# Revit family: NLRS_33_RB_DO_BILCO_dakluik_GS-50TB
name_source: partatom
category: Doors
revit_build: Autodesk Revit 2015 (Build: 20140223_1515(x64)
units: mm (PartAtom-declared; Revit-internal decimal feet)

## types (1)
- NLRS_33_RB_DO_BILCO_dakluik_GS-50TB
    Description = standaard dakluik met polycarbonaat koepel
    Height = 535 mm
    Length = 1040 mm  [stored 3.41207 ft]
    Manufacturer = Bilco
    RWA = No
    Rough Height = 0 mm  [stored 0 ft]
    Rough Width = 0 mm  [stored 0 ft]
    Thickness = 0 mm  [stored 0 ft]
    Width = 1195 mm  [stored 3.9206 ft]
    bediening = handmatig
    belasting = 195.00 kg/m²
    brandwerend 120 min = No
    brandwerend 30 min = No
    brandwerend 60 min = No
    brandwerend 90 min = No
    breedte = 1195 mm  [stored 3.9206 ft]
    breedte_koepel = 981 mm  [stored 3.2185 ft]
    breedte_paneel = 1105 mm  [stored 3.62533 ft]
    cilinderslot = No
    code productgroep = dakluiken
    conservering = brut
    dagmaatbreedte = 915 mm  [stored 3.00197 ft]
    dagmaatlengte = 760 mm  [stored 2.49344 ft]
    dikte_isolatie = 0 mm  [stored 0 ft]
    false = No
    gewicht (kg) = 64
    hoogte = 535 mm
    hoogte_aandrijving = 323 mm  [stored 1.05971 ft]
    hoogte_frame = 400 mm  [stored 1.31234 ft]
    hoogte_opstand = 305 mm  [stored 1.00066 ft]
    inbouwhoogte = 0 mm  [stored 0 ft]
    isolatie = Yes
    isolatiedikte = 75 mm
    isolatiewaarde = 3.5900 (m²·K)/W
    lengte = 1040 mm  [stored 3.41207 ft]
    lengte maximaal = 0 mm  [stored 0 ft]
    lengte minimaal = 0 mm  [stored 0 ft]
    lengte_koepel = 826 mm
    lengte_paneel = 950 mm  [stored 3.1168 ft]
    loopslot = Yes
    materiaal = bcb_aluminium
    materiaal_secundair = bcb_pc
    omranding dakopstand = Yes
    omranding hoekprofiel = No
    omranding waterafvoerend = No
    omschrijving = standaard dakluik met polycarbonaat koepel
    openingshoek = 70.00°
    openstand vergrendeling = Yes
    plaatdikte = 2 mm  [stored 0.00656168 ft]
    productgroep = LUI
    thermische onderbreking = Yes
    true = Yes
    veersysteem = Yes
    waterdicht = Yes

note: [stored X ft] marks values corroborated as IEEE doubles in the binary element streams (Revit-internal decimal feet)

## geometry (parser evidence)
native form markers: Blend x565, Sweep x13
no freeform markers — native parametric forms only
